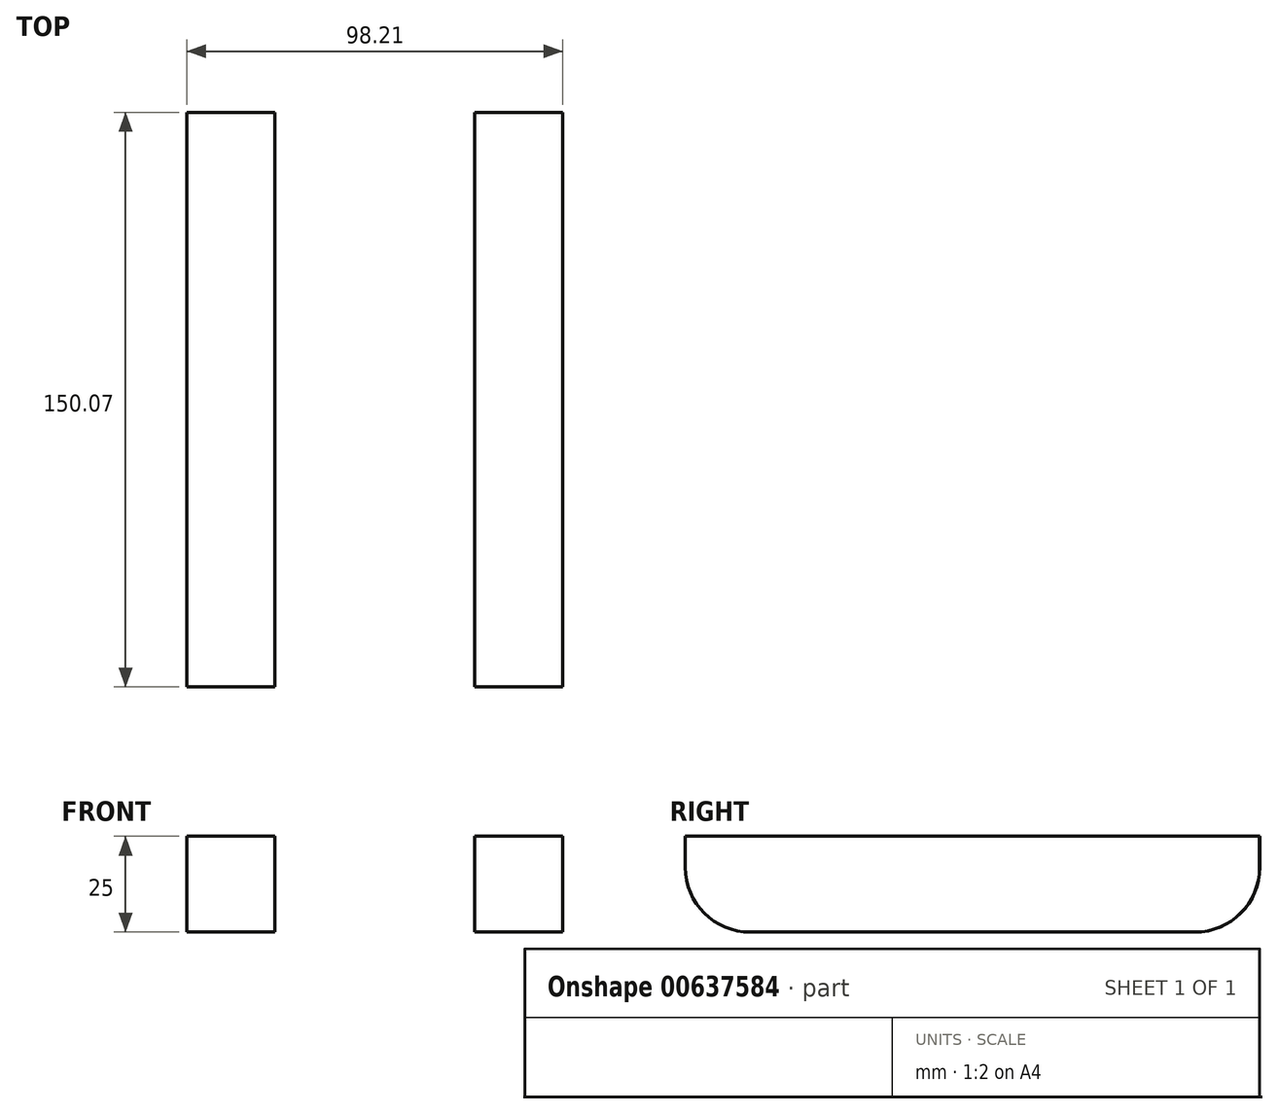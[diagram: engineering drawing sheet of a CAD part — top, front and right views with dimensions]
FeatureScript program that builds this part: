
annotation { "Feature Type Name" : "Feature", "Feature Type Description" : "" }
export const myFeature = defineFeature(function(context is Context, id is Id, definition is map)
    precondition{}
    {
        {
            var Q0;
            Q0=qCreatedBy(makeId("Top.planeOp"),FACE);
            var sketch = newSketch(context, id + "F0", { "sketchPlane" : qUnion([Q0])});
            skLineSegment(sketch, "E0.bottom", {"start": v(-54.69, 75.07) * mm, "end": v(-31.69, 75.07) * mm});
            skLineSegment(sketch, "E0.top", {"start": v(-54.69, -75) * mm, "end": v(-31.69, -75) * mm});
            skLineSegment(sketch, "E0.left", {"start": v(-54.69, 75.07) * mm, "end": v(-54.69, -75) * mm});
            skLineSegment(sketch, "E0.right", {"start": v(-31.69, 75.07) * mm, "end": v(-31.69, -75) * mm});
            skLineSegment(sketch, "E1.bottom", {"start": v(20.52, 75) * mm, "end": v(43.52, 75) * mm});
            skLineSegment(sketch, "E1.top", {"start": v(20.52, -75) * mm, "end": v(43.52, -75) * mm});
            skLineSegment(sketch, "E1.left", {"start": v(20.52, 75) * mm, "end": v(20.52, -75) * mm});
            skLineSegment(sketch, "E1.right", {"start": v(43.52, 75) * mm, "end": v(43.52, -75) * mm});
            skSolve(sketch);
        }
        {
            var Q0;
            Q0=makeQuery(id+"F0.imprint","IMPRINT",FACE,{"disambiguationData":[TD([[makeQuery(id+"F0.imprint","IMPRINT",EDGE,{"derivedFrom":sQuery(id+"F0.wireOp",EDGE,"E0.bottom")}),-1.0]])]});
            var Q1;
            Q1=makeQuery(id+"F0.imprint","IMPRINT",FACE,{"disambiguationData":[TD([[makeQuery(id+"F0.imprint","IMPRINT",EDGE,{"derivedFrom":sQuery(id+"F0.wireOp",EDGE,"E1.bottom")}),-1.0]])]});
            extrude(context, id + "F1", {"entities" : qUnion([Q0, Q1]), "depth" : 25 * mm, "offsetDistance" : 25 * mm});
        }
        {
            var Q0;
            Q0=makeQuery(id+"F1.opExtrude","CAP_EDGE",EDGE,{"disambiguationData":[OSD([sQuery(id+"F0.wireOp",EDGE,"E0.top")])],"isStart":true});
            var Q1;
            Q1=makeQuery(id+"F1.opExtrude","CAP_EDGE",EDGE,{"disambiguationData":[OSD([sQuery(id+"F0.wireOp",EDGE,"E1.top")])],"isStart":true});
            var Q2;
            Q2=makeQuery(id+"F1.opExtrude","CAP_EDGE",EDGE,{"disambiguationData":[OSD([sQuery(id+"F0.wireOp",EDGE,"E0.bottom")])],"isStart":true});
            var Q3;
            Q3=makeQuery(id+"F1.opExtrude","CAP_EDGE",EDGE,{"disambiguationData":[OSD([sQuery(id+"F0.wireOp",EDGE,"E1.bottom")])],"isStart":true});
            fillet(context, id + "F2", {"entities" : qUnion([Q0, Q1, Q2, Q3]), "radius" : 16.9 * mm, "tangentPropagation" : true, "allowEdgeOverflow" : false});
        }
    });
